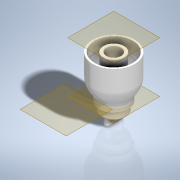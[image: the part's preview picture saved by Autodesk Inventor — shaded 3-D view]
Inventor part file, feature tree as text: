
AUTODESK INVENTOR PART (.ipt)
format: ipt  version: 2020.1 (Build 241239000, 239)  size: 504,832 bytes
history: native  units: mm
features: sketch x11, fillet x10, extrude x8, plane x5, loft x2, delete_face x2, other x2, shell x1, split x1, hole x1
ambient origin geometry x8: Origin, YZ Plane, XZ Plane, XY Plane, X Axis, Y Axis, Z Axis, Center Point
bodies: Solid1 (feature_tree), Solid2 (feature_tree), Solid3 (feature_tree)
feature tree (43):
  extrude  "Extrusion1"  Depth=70.0mm TaperAngle=0.0deg
  plane  "Work Plane1"
  loft  "Loft1"
  fillet  "Fillet1"  Radius=25.0mm
  plane  "Work Plane2"
  loft  "Loft2"
  shell  "Shell1"  Thickness=0.0mm
  extrude  "Extrusion2"  Depth=2.5mm
  fillet  "Fillet2"  Radius=33.0mm
  extrude  "Extrusion3"  Depth=25.0mm
  extrude  "Extrusion4"  Depth=10.0mm
  fillet  "Fillet5"  Radius=8.0mm
  fillet  "Fillet7"  Radius=8.0mm
  split  "Split1"
  delete_face  "Delete Face1"
  delete_face  "Delete Face2"
  fillet  "Fillet8"  Radius=10.0mm
  fillet  "Fillet9"  Radius=8.0mm
  plane  "Work Plane3"
  plane  "Work Plane4"
  extrude  "Extrusion8"  Depth=3.0mm
  extrude  "Extrusion7"  Depth=10.0mm
  hole  "Hole4"  [1 undecoded]
  plane  "Work Plane5"
  extrude  "Extrusion11"  [1 undecoded]
  fillet  "Fillet19"  Radius=8.5mm
  fillet  "Fillet20"  Radius=8.5mm
  fillet  "Fillet21"  Radius=10.0mm
  extrude  "Extrusion12"  Depth=10.0mm TaperAngle=0.0deg
  fillet  "Fillet22"  Radius=4.25mm
  sketch  "Sketch1"  dims[d0=55.0mm d1=70.0mm d2=0.0mm]
  sketch  "Sketch4"  dims[d4=75.0mm d5=0.0mm d6=90.0deg d7=5.0mm d8=90.0deg d9=25.0mm]
  other  "Edges1"
  sketch  "Sketch5"  dims[d10=20.0mm d11=30.0mm d12=0.0mm d13=90.0deg]
  other  "Edges2"
  sketch  "Sketch6"  dims[d14=0.0mm d15=90.0deg d16=2.5mm d17=33.0mm]
  sketch  "Sketch7"  dims[d18=15.0mm d19=0.0mm d20=25.0mm]
  sketch  "Sketch8"  dims[d21=8.0mm d22=8.0mm d23=8.0mm d24=8.0mm d25=10.0mm d26=0.0mm d27=8.0mm]
  sketch  "Sketch13"  dims[d28=24.0mm d29=0.0mm d32=3.0mm]
  sketch  "Sketch16"  dims[d34=10.0mm d35=10.0mm]
  sketch  "Sketch17"  dims[d36=10.0mm d37=10.0mm]
  sketch  "Sketch20"  dims[d38=10.0mm d84=-45.0mm d85=8.5mm d86=8.5mm d87=10.0mm d88=0.0mm]
  sketch  "Sketch21"  dims[d111=3.0mm d112=22.0mm d113=0.0mm d114=4.25mm d115=4.25mm d116=4.25mm d117=4.25mm d118=5.0mm d119=6.0mm d120=4.0mm d121=2.0mm d122=90.0deg d123=8.0mm d124=20.594885mm d125=-53.0mm d126=4.0mm d127=20.0mm d128=53.0mm d129=0.0mm d131=5.0mm d132=0.0mm d152=69.75mm d153=2.0mm d154=35.0mm d155=0.0mm d157=0.0mm d158=3.5mm d159=3.5mm d160=2.0mm d161=34.0mm d162=3.0mm d163=5.0mm d164=0.0mm d165=10.0mm]
note: 2 required parameter values undecoded (feature->parameter linkage not recoverable at this tier; creation-order binding heuristic only, values carry confidence <= 0.55)
